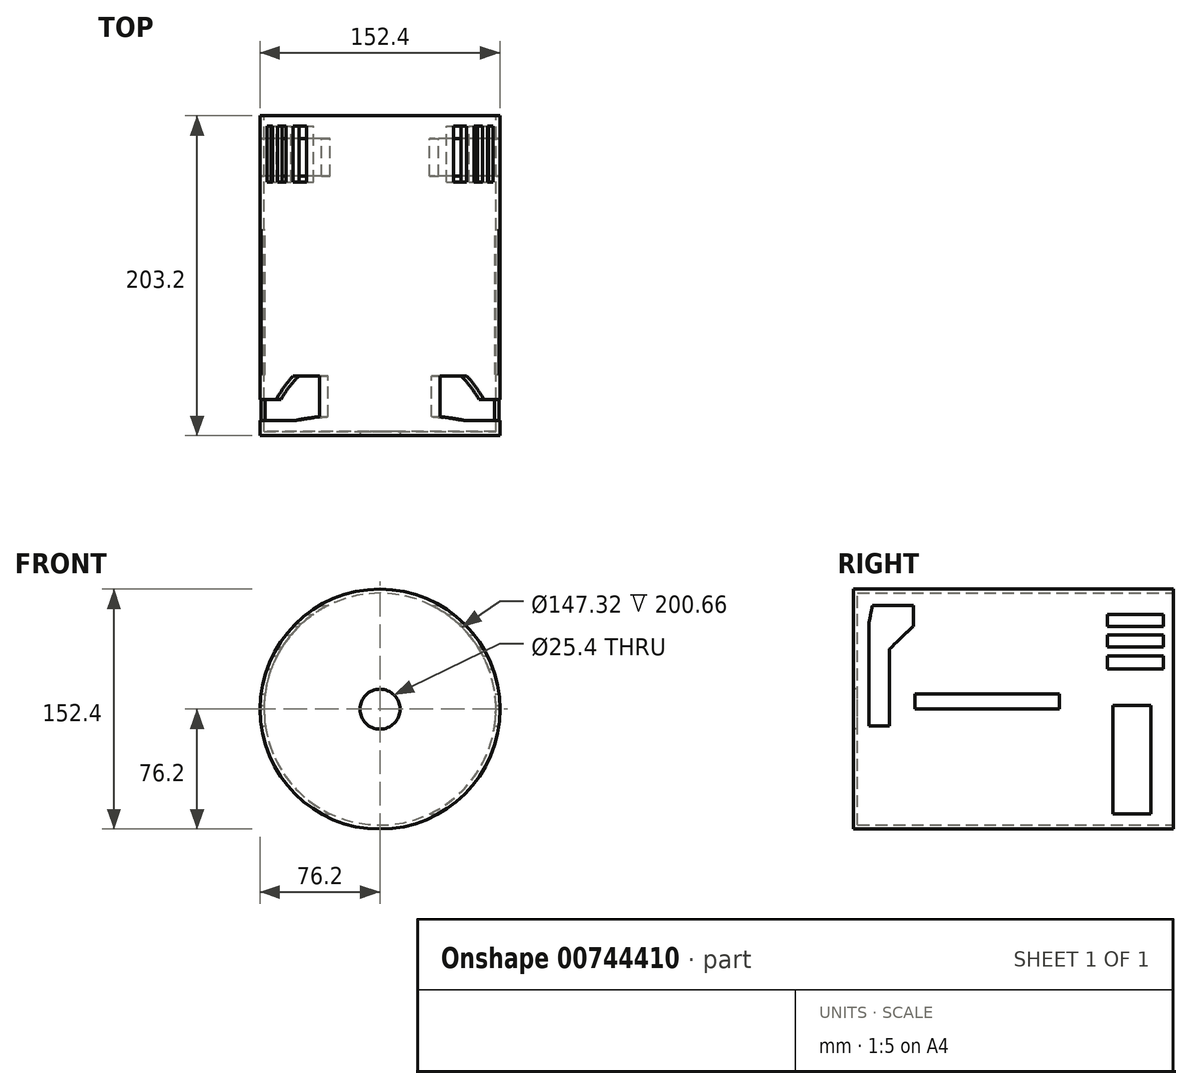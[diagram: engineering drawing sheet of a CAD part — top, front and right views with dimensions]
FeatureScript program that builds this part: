
annotation { "Feature Type Name" : "Feature", "Feature Type Description" : "" }
export const myFeature = defineFeature(function(context is Context, id is Id, definition is map)
    precondition{}
    {
        {
            var Q0;
            Q0=qCreatedBy(makeId("Front.planeOp"),FACE);
            var sketch = newSketch(context, id + "F0", { "sketchPlane" : qUnion([Q0])});
            skCircle(sketch, "E0", {"center": v(0, 0) * mm, "radius": 76.2 * mm});
            skSolve(sketch);
        }
        {
            var Q0;
            Q0=qSketchRegion(id+"F0",true);
            extrude(context, id + "F1", {"entities" : qUnion([Q0]), "depth" : 203.2 * mm});
        }
        {
            var Q0;
            Q0=makeQuery(id+"F1.opExtrude","CAP_FACE",FACE,{"disambiguationData":[OSD([sQuery(id+"F0.wireOp",EDGE,"E0")])],"isStart":false});
            var sketch = newSketch(context, id + "F2", { "sketchPlane" : qUnion([Q0])});
            skCircle(sketch, "E1", {"center": v(0, 0) * mm, "radius": 12.7 * mm});
            skSolve(sketch);
        }
        {
            var Q0;
            Q0=qSketchRegion(id+"F2",true);
            extrude(context, id + "F3", {"entities" : qUnion([Q0]), "operationType" : NewBodyOperationType.ADD, "depth" : 38.1 * mm});
        }
        {
            var Q0;
            Q0=makeQuery(id+"F1.opExtrude","CAP_FACE",FACE,{"disambiguationData":[OSD([sQuery(id+"F0.wireOp",EDGE,"E0")])],"isStart":true});
            shell(context, id + "F4", {"entities" : qUnion([Q0]), "thickness" : 2.54 * mm});
        }
        {
            var Q0;
            Q0=qCreatedBy(makeId("Right.planeOp"),FACE);
            var sketch = newSketch(context, id + "F5", { "sketchPlane" : qUnion([Q0])});
            skLineSegment(sketch, "E2", {"start": v(-191.12, 65.91) * mm, "end": v(-165.21, 65.91) * mm});
            skLineSegment(sketch, "E3", {"start": v(-165.21, 65.91) * mm, "end": v(-165.21, 52.67) * mm});
            skLineSegment(sketch, "E4", {"start": v(-165.21, 52.67) * mm, "end": v(-180.18, 38.28) * mm});
            skLineSegment(sketch, "E5", {"start": v(-180.18, 38.28) * mm, "end": v(-180.18, -10.65) * mm});
            skLineSegment(sketch, "E6", {"start": v(-180.18, -10.65) * mm, "end": v(-193.42, -10.65) * mm});
            skLineSegment(sketch, "E7", {"start": v(-193.42, -10.65) * mm, "end": v(-193.42, 54.4) * mm});
            skLineSegment(sketch, "E8", {"start": v(-193.42, 54.4) * mm, "end": v(-191.12, 65.91) * mm});
            skLineSegment(sketch, "E9.bottom", {"start": v(-6.46, 52.67) * mm, "end": v(-42.02, 52.67) * mm});
            skLineSegment(sketch, "E9.top", {"start": v(-6.46, 60.3) * mm, "end": v(-42.02, 60.3) * mm});
            skLineSegment(sketch, "E9.left", {"start": v(-6.46, 52.67) * mm, "end": v(-6.46, 60.3) * mm});
            skLineSegment(sketch, "E9.right", {"start": v(-42.02, 52.67) * mm, "end": v(-42.02, 60.3) * mm});
            skPoint(sketch, "E9.middle", {"position": v(-24.24, 56.48) * mm});
            skLineSegment(sketch, "E10.bottom", {"start": v(-6.46, 39.65) * mm, "end": v(-42.02, 39.65) * mm});
            skLineSegment(sketch, "E10.top", {"start": v(-6.46, 47.27) * mm, "end": v(-42.02, 47.27) * mm});
            skLineSegment(sketch, "E10.left", {"start": v(-6.46, 39.65) * mm, "end": v(-6.46, 47.27) * mm});
            skLineSegment(sketch, "E10.right", {"start": v(-42.02, 39.65) * mm, "end": v(-42.02, 47.27) * mm});
            skPoint(sketch, "E10.middle", {"position": v(-24.24, 43.46) * mm});
            skLineSegment(sketch, "E11.bottom", {"start": v(-6.46, 25.62) * mm, "end": v(-42.02, 25.62) * mm});
            skLineSegment(sketch, "E11.top", {"start": v(-6.46, 33.68) * mm, "end": v(-42.02, 33.68) * mm});
            skLineSegment(sketch, "E11.left", {"start": v(-6.46, 25.62) * mm, "end": v(-6.46, 33.68) * mm});
            skLineSegment(sketch, "E11.right", {"start": v(-42.02, 25.62) * mm, "end": v(-42.02, 33.68) * mm});
            skPoint(sketch, "E11.middle", {"position": v(-24.24, 29.65) * mm});
            skSolve(sketch);
        }
        {
            var Q0;
            Q0=makeQuery(id+"F5.imprint","IMPRINT",FACE,{"disambiguationData":[TD([[makeQuery(id+"F5.imprint","IMPRINT",EDGE,{"derivedFrom":sQuery(id+"F5.wireOp",EDGE,"E9.bottom")}),-1.0]])]});
            var Q1;
            Q1=makeQuery(id+"F5.imprint","IMPRINT",FACE,{"disambiguationData":[TD([[makeQuery(id+"F5.imprint","IMPRINT",EDGE,{"derivedFrom":sQuery(id+"F5.wireOp",EDGE,"E10.bottom")}),-1.0]])]});
            var Q2;
            Q2=makeQuery(id+"F5.imprint","IMPRINT",FACE,{"disambiguationData":[TD([[makeQuery(id+"F5.imprint","IMPRINT",EDGE,{"derivedFrom":sQuery(id+"F5.wireOp",EDGE,"E11.bottom")}),-1.0]])]});
            var Q3;
            Q3=makeQuery(id+"F5.imprint","IMPRINT",FACE,{"disambiguationData":[TD([[makeQuery(id+"F5.imprint","IMPRINT",EDGE,{"derivedFrom":sQuery(id+"F5.wireOp",EDGE,"E2")}),-1.0]])]});
            extrude(context, id + "F6", {"entities" : qUnion([Q0, Q1, Q2, Q3]), "operationType" : NewBodyOperationType.REMOVE, "endBound" : BoundingType.SYMMETRIC, "oppositeDirection" : true, "depth" : 177.8 * mm});
        }
        {
            var Q0;
            Q0=makeQuery(id+"F3.opExtrude","CAP_FACE",FACE,{"disambiguationData":[OSD([sQuery(id+"F2.wireOp",EDGE,"E1")])],"isStart":false});
            var sketch = newSketch(context, id + "F7", { "sketchPlane" : qUnion([Q0])});
            skSolve(sketch);
        }
        {
            var Q0;
            Q0=makeQuery(id+"F7.imprint","IMPRINT",FACE,{"disambiguationData":[TD([[makeQuery(id+"F7.imprint","IMPRINT",EDGE,{"derivedFrom":makeQuery(id+"F3.opExtrude","CAP_EDGE",EDGE,{"disambiguationData":[OSD([sQuery(id+"F2.wireOp",EDGE,"E1")])],"isStart":false})}),1.0]])]});
            extrude(context, id + "F8", {"entities" : qUnion([Q0]), "operationType" : NewBodyOperationType.REMOVE, "endBound" : BoundingType.THROUGH_ALL, "oppositeDirection" : true, "depth" : 25.4 * mm});
        }
        {
            var Q0;
            Q0=qCreatedBy(makeId("Right.planeOp"),FACE);
            var sketch = newSketch(context, id + "F9", { "sketchPlane" : qUnion([Q0])});
            skLineSegment(sketch, "E12.bottom", {"start": v(-14.34, -66.53) * mm, "end": v(-38.38, -66.53) * mm});
            skLineSegment(sketch, "E12.top", {"start": v(-14.34, 2.4) * mm, "end": v(-38.38, 2.4) * mm});
            skLineSegment(sketch, "E12.left", {"start": v(-14.34, -66.53) * mm, "end": v(-14.34, 2.4) * mm});
            skLineSegment(sketch, "E12.right", {"start": v(-38.38, -66.53) * mm, "end": v(-38.38, 2.4) * mm});
            skPoint(sketch, "E12.middle", {"position": v(-26.36, -32.07) * mm});
            skLineSegment(sketch, "E13.bottom", {"start": v(-72.32, 0) * mm, "end": v(-164.23, 0) * mm});
            skLineSegment(sketch, "E13.top", {"start": v(-72.32, 9.61) * mm, "end": v(-164.23, 9.61) * mm});
            skLineSegment(sketch, "E13.left", {"start": v(-72.32, 0) * mm, "end": v(-72.32, 9.61) * mm});
            skLineSegment(sketch, "E13.right", {"start": v(-164.23, 0) * mm, "end": v(-164.23, 9.61) * mm});
            skPoint(sketch, "E13.middle", {"position": v(-118.27, 4.8) * mm});
            skSolve(sketch);
        }
        {
            var Q0;
            Q0=qSketchRegion(id+"F9",true);
            extrude(context, id + "F10", {"entities" : qUnion([Q0]), "operationType" : NewBodyOperationType.REMOVE, "endBound" : BoundingType.SYMMETRIC, "oppositeDirection" : true, "depth" : 254 * mm});
        }
    });
